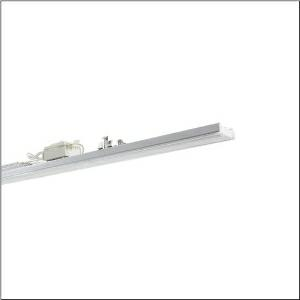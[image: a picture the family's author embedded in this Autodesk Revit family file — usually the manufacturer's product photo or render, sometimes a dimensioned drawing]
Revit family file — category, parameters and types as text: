
# Revit family: licross_r__11_recessed_ho_51te1emn4d5s_0657
name_source: partatom
category: Lighting Fixtures
units: mm (PartAtom-declared; Revit-internal decimal feet)

## family parameters
Cut with Voids When Loaded = No
Host = Face
Light Source = No
Part Type = Normal
Room Calculation Point = No
Round Connector Dimension = Use Diameter
Shared = No

## types (1)
- --- (1 x LED, 13740 lm, 74.5 W, 4000K)
    Apparent Load = 75 VA
    CIE Flux Codes = 85 95 99 100 100
    Color Rendering = 80
    Color Temperature = 4000K
    Default Elevation = 1800 mm
    Description = Licross® 11 Recessed HO, luminaire insert, of sheet steel, galvanised, coil coated, white, length: 1.500mm, width: 66mm, height: 67mm, LED rated luminous flux: 13.740lm, light colour: 840, control gear: ON/OFF Multilumen, with plug, 3-pole, with phase selection, mains connection: 220..240V, AC, 50/60Hz, rated input power: 75W, halogen-free wiring, primary light control with lens, of plastic, primary optical cover: cover, of PMMA, light emission: direct distribution, primary light characteristic: symmetric, protection rating (complete): IP54, insulation class (complete): insulation class I (protective earthing), certification: CE, ENEC, VDE, UKCA, protection symbol: D if used in an environment with non-conductive dust loads with corresponding accessories, impact resistance: IK06, permissible ambient temperature for indoor applications: -35..+35°C, corresponds to IFS (International Featured Standards) requirements for safety and quality in the food industry, reducing of maximum allowable ambient temperature of 5°C with ceiling mounting, packaging unit: 1 piece
    Height = 58 mm
    Lamp = 1 x LED
    Lamp Light Flux = 13740 lm
    Lamp Power = 74.5 W
    Lamp count = 1
    Length = 1500 mm
    Luminous efficacy = 184 lm/W
    Manufacturer = Siteco
    ModVariant = No
    Model = 51TE1EMN4D5S
    Mounting Place = Ceiling
    Mounting Type = Pendant
    Number of Poles = 1
    OnlyDefault = Yes
    Power Factor = 1
    Product Name = Licross® 11 Recessed HO
    Product group = luminaire insert
    ProductGroupID = 902
    Protection Class = Protection class I
    Protection Degree = IP 54
    RLX_Detail_Level = 1
    RLX_Emergency_Light_Flux = 0 lm
    RLX_Emergency_Type = 0
    RLX_Emergency_Type_DB = No
    RlxData = <blob elided: 22309 chars, md5=41e075ee>
    Socket = socket
    Standby Power = 0 W
    System Light Flux = 13740 lm
    System Power = 75 W
    Type Comments = factory setting: luminous flux: 100 % | (A | C | E) | 174 mA
    Type Image = l_1296930.jpg
    URL = http://relux.com
    VarID = @adj_084292
    Voltage = 0 V
    Weight = 0.00 kg
    Width = 66 mm

## geometry (parser evidence)
native form markers: Blend x4, Sweep x12
no freeform markers — native parametric forms only
